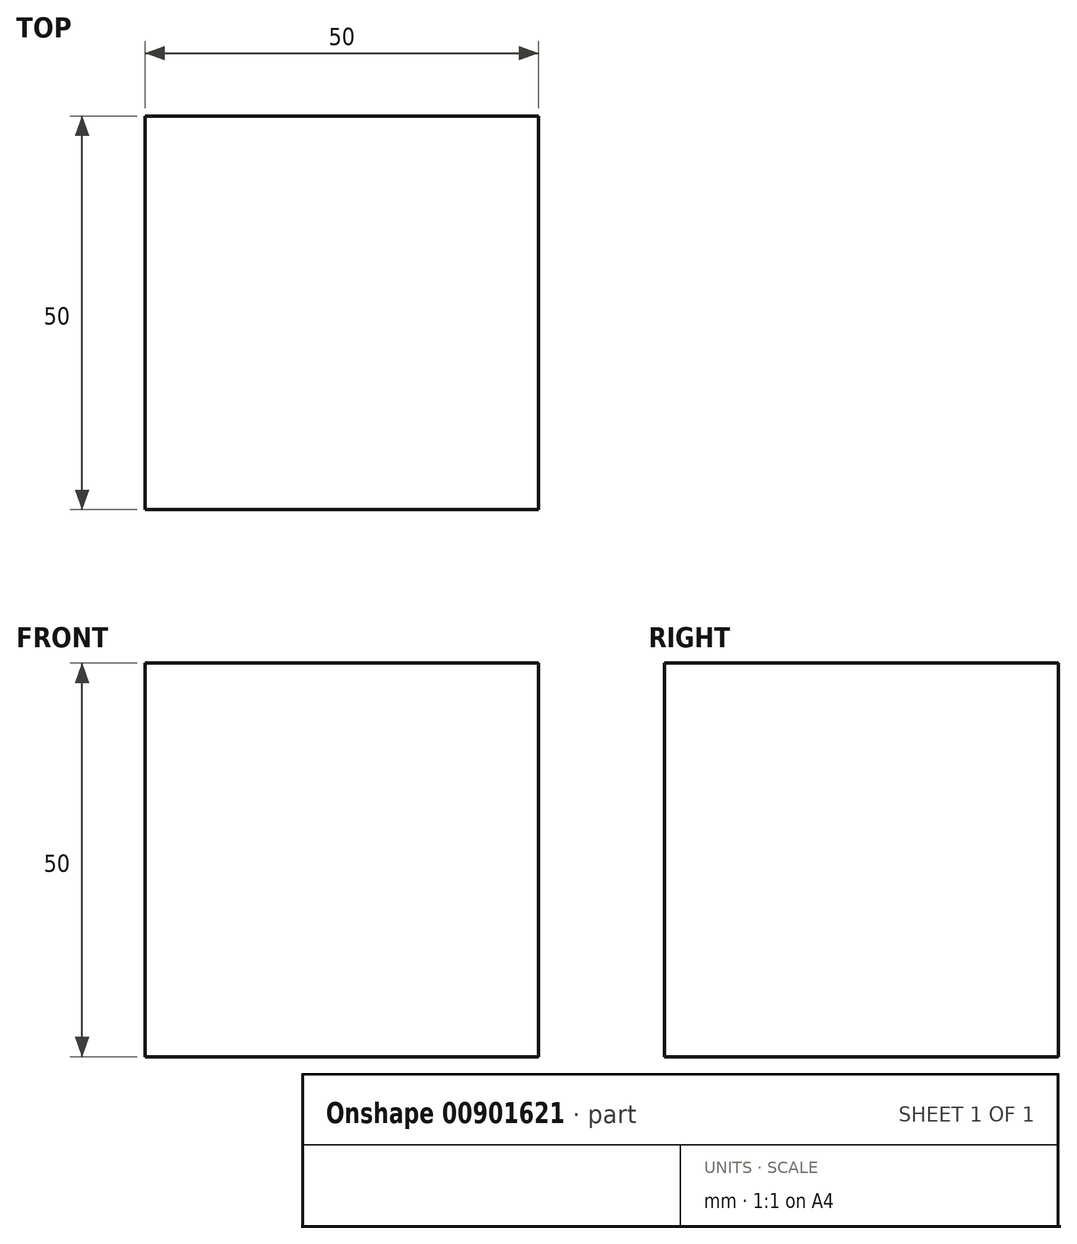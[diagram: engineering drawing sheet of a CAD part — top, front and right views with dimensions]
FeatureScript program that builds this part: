
annotation { "Feature Type Name" : "Feature", "Feature Type Description" : "" }
export const myFeature = defineFeature(function(context is Context, id is Id, definition is map)
    precondition{}
    {
        {
            var Q0;
            Q0=qCreatedBy(makeId("Front.planeOp"),FACE);
            var sketch = newSketch(context, id + "F0", { "sketchPlane" : qUnion([Q0])});
            skLineSegment(sketch, "E0.bottom", {"start": v(25, 25) * mm, "end": v(-25, 25) * mm});
            skLineSegment(sketch, "E0.top", {"start": v(25, -25) * mm, "end": v(-25, -25) * mm});
            skLineSegment(sketch, "E0.left", {"start": v(25, 25) * mm, "end": v(25, -25) * mm});
            skLineSegment(sketch, "E0.right", {"start": v(-25, 25) * mm, "end": v(-25, -25) * mm});
            skPoint(sketch, "E0.middle", {"position": v(0, 0) * mm});
            skSolve(sketch);
        }
        {
            var Q0;
            Q0 = qSketchRegion(id + "F0", true);
            extrude(context, id + "F1", {"entities" : qUnion([Q0]), "endBound" : BoundingType.SYMMETRIC, "depth" : 50 * mm, "offsetDistance" : 25 * mm});
        }
    });
